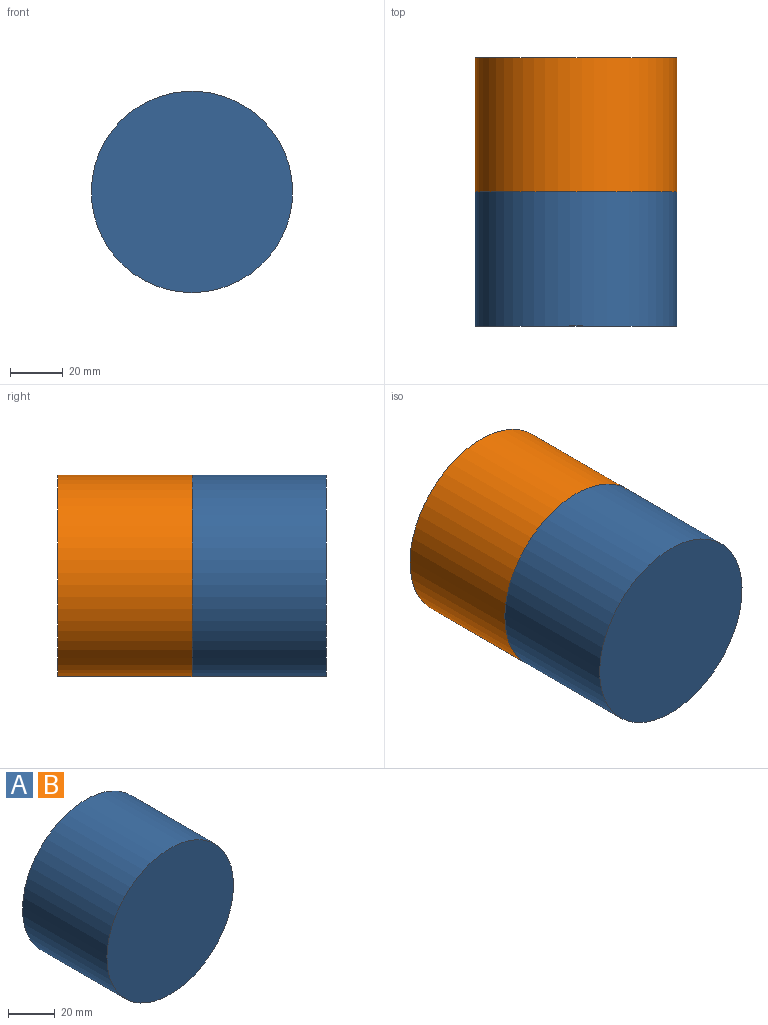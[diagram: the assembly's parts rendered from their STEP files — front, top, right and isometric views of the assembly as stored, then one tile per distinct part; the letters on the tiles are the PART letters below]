
ASSEMBLY  parts=2 mates=1
PART A: 3 faces, bbox 76.2x50.8x76.2 mm
  f0: cylinder r=38.1mm len=76.2mm, axis (0,1,0), area 12161mm2, adj f1,f2
  f1: plane 76.2x76.2mm, normal (0,-1,0), area 4560.4mm2, adj f0
  f2: plane 76.2x76.2mm, normal (0,1,0), area 4560.4mm2, adj f0
PART B: same geometry as A
PLACE A t=(-17.43,-12.62,11.95)mm
PLACE B t=(-17.43,38.18,11.95)mm
MATE slider B.f0 <-> A.f0  axis (0,-1,0) through (-17.43,-12.62,11.95)mm
